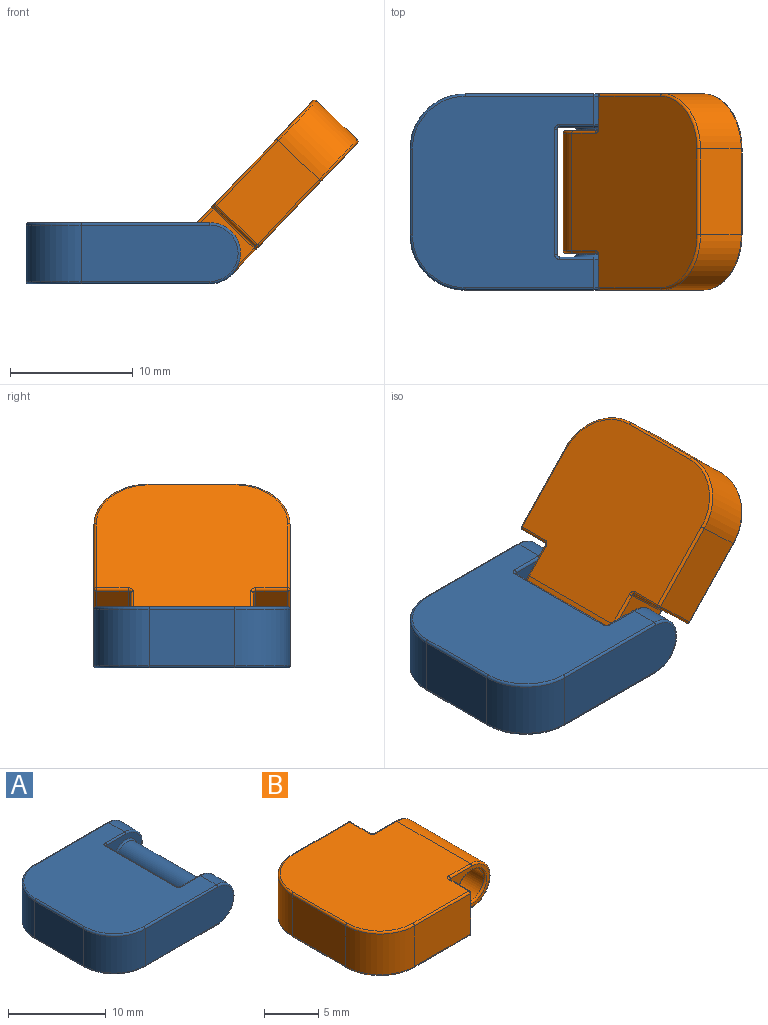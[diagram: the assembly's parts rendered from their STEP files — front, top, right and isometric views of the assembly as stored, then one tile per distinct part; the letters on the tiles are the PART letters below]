
ASSEMBLY  parts=2 mates=1
PART A: 41 faces, bbox 18.1x16.7x5.4 mm
  f0: plane 15.6x14.8mm, normal (0,0,-1), area 187.8mm2, adj f1,f8,f19,f21,f22,f23,f24,f29
  f1: cylinder r=2.5mm len=5mm, axis (0,1,0), area 18.1mm2, adj f0,f2,f17,f26
  f2: plane 15.6x14.8mm, normal (0,0,1), area 187.8mm2, adj f1,f8,f13,f14,f15,f16,f18,f27
  f3: plane 7x4.6mm, normal (-1,0,0), area 32.2mm2, adj f11,f12,f14,f23
  f4: plane 5.1x4.6mm, normal (0,-1,0), area 12.6mm2, adj f26,f27,f28,f29,f40
  f5: plane 12.8x4.6mm, normal (0,1,0), area 56.6mm2, adj f12,f15,f17,f19
  f6: plane 10.2x4.6mm, normal (1,0,0), area 46.9mm2, adj f28,f32,f33,f34
  f7: cylinder r=1.45mm len=10.2mm, axis (0,1,0), area 92.9mm2, adj f25,f40
  f8: cylinder r=2.5mm len=5mm, axis (0,-1,0), area 18.1mm2, adj f0,f2,f20,f39
  f9: plane 5.1x4.6mm, normal (0,1,0), area 12.6mm2, adj f25,f33,f37,f38,f39
  f10: plane 12.8x4.6mm, normal (0,-1,0), area 56.6mm2, adj f11,f18,f20,f22
  f11: cylinder r=4.5mm len=4.6mm, axis (0,0,-1), area 32.5mm2, adj f3,f10,f16,f24
  f12: cylinder r=4.5mm len=4.6mm, axis (0,0,-1), area 32.5mm2, adj f3,f5,f13,f21
  f13: torus R=4.3mm, axis (0,0,-1), area 2.2mm2, adj f2,f12,f14,f15
  f14: cylinder r=0.2mm len=7mm, axis (0,-1,0), area 2.2mm2, adj f2,f3,f13,f16
  f15: cylinder r=0.2mm len=10.5mm, axis (-1,0,0), area 3.3mm2, adj f2,f5,f13,f17
  f16: torus R=4.3mm, axis (0,0,-1), area 2.2mm2, adj f2,f11,f14,f18
  f17: torus R=2.3mm, axis (0,-1,0), area 2.4mm2, adj f1,f5,f15,f19
  f18: cylinder r=0.2mm len=10.5mm, axis (-1,0,0), area 3.3mm2, adj f2,f10,f16,f20
  f19: cylinder r=0.2mm len=10.5mm, axis (1,0,0), area 3.3mm2, adj f0,f5,f17,f21
  f20: torus R=2.3mm, axis (0,1,0), area 2.4mm2, adj f8,f10,f18,f22
  f21: torus R=4.3mm, axis (0,0,-1), area 2.2mm2, adj f0,f12,f19,f23
  f22: cylinder r=0.2mm len=10.5mm, axis (1,0,0), area 3.3mm2, adj f0,f10,f20,f24
  f23: cylinder r=0.2mm len=7mm, axis (0,1,0), area 2.2mm2, adj f0,f3,f21,f24
  f24: torus R=4.3mm, axis (0,0,-1), area 2.2mm2, adj f0,f11,f22,f23
  f25: torus R=1.65mm, axis (0,1,0), area 3mm2, adj f7,f9
  f26: torus R=2.3mm, axis (0,-1,0), area 2.4mm2, adj f1,f4,f27,f29
  f27: cylinder r=0.2mm len=2.8mm, axis (1,0,0), area 0.9mm2, adj f2,f4,f26,f30
  f28: cylinder r=0.2mm len=4.6mm, axis (0,0,-1), area 1.4mm2, adj f4,f6,f30,f31
  f29: cylinder r=0.2mm len=2.8mm, axis (-1,0,0), area 0.9mm2, adj f0,f4,f26,f31
  f30: torus R=0.4mm, axis (0,0,-1), area 0.1mm2, adj f2,f27,f28,f32
  f31: torus R=0.4mm, axis (0,0,-1), area 0.1mm2, adj f0,f28,f29,f34
  f32: cylinder r=0.2mm len=10.2mm, axis (0,-1,0), area 3.2mm2, adj f2,f6,f30,f35
  f33: cylinder r=0.2mm len=4.6mm, axis (0,0,-1), area 1.4mm2, adj f6,f9,f35,f36
  f34: cylinder r=0.2mm len=10.2mm, axis (0,1,0), area 3.2mm2, adj f0,f6,f31,f36
  f35: torus R=0.4mm, axis (0,0,-1), area 0.1mm2, adj f2,f32,f33,f37
  f36: torus R=0.4mm, axis (0,0,-1), area 0.1mm2, adj f0,f33,f34,f38
  f37: cylinder r=0.2mm len=2.8mm, axis (1,0,0), area 0.9mm2, adj f2,f9,f35,f39
  f38: cylinder r=0.2mm len=2.8mm, axis (-1,0,0), area 0.9mm2, adj f0,f9,f36,f39
  f39: torus R=2.3mm, axis (0,1,0), area 2.4mm2, adj f8,f9,f37,f38
  f40: torus R=1.65mm, axis (0,-1,0), area 3mm2, adj f4,f7
PART B: 47 faces, bbox 18.1x16.7x5.4 mm
  f0: plane 5.1x4.6mm, normal (0,-1,0), area 9.2mm2, adj f18,f25,f30,f31,f46
  f1: plane 5.1x4.6mm, normal (0,1,0), area 9.2mm2, adj f13,f14,f19,f20,f45
  f2: plane 15.6x14.8mm, normal (0,0,-1), area 203.8mm2, adj f3,f19,f26,f31,f32,f35,f38,f39
  f3: cylinder r=2.5mm len=9.6mm, axis (0,1,0), area 75.4mm2, adj f2,f4,f14,f25
  f4: plane 15.6x14.8mm, normal (0,0,1), area 203.8mm2, adj f3,f13,f15,f16,f17,f18,f21,f22
  f5: plane 7x4.6mm, normal (-1,0,0), area 32.2mm2, adj f11,f12,f17,f43
  f6: cylinder r=1.75mm len=9.6mm, axis (0,1,0), area 105.6mm2, adj f45,f46
  f7: plane 4.6x2.6mm, normal (1,0,0), area 12mm2, adj f20,f21,f32,f33
  f8: plane 7.3x4.6mm, normal (0,1,0), area 33.6mm2, adj f12,f22,f33,f39
  f9: plane 4.6x2.6mm, normal (1,0,0), area 12mm2, adj f29,f30,f37,f38
  f10: plane 7.3x4.6mm, normal (0,-1,0), area 33.6mm2, adj f11,f28,f37,f42
  f11: cylinder r=4.5mm len=4.6mm, axis (0,0,-1), area 32.5mm2, adj f5,f10,f23,f44
  f12: cylinder r=4.5mm len=4.6mm, axis (0,0,-1), area 32.5mm2, adj f5,f8,f16,f41
  f13: cylinder r=0.2mm len=2.8mm, axis (-1,0,0), area 0.9mm2, adj f1,f4,f14,f15
  f14: torus R=2.3mm, axis (0,-1,0), area 2.4mm2, adj f1,f3,f13,f19
  f15: torus R=0.4mm, axis (0,0,-1), area 0.1mm2, adj f4,f13,f20,f21
  f16: torus R=4.3mm, axis (0,0,-1), area 2.2mm2, adj f4,f12,f17,f22
  f17: cylinder r=0.2mm len=7mm, axis (0,-1,0), area 2.2mm2, adj f4,f5,f16,f23
  f18: cylinder r=0.2mm len=2.8mm, axis (1,0,0), area 0.9mm2, adj f0,f4,f24,f25
  f19: cylinder r=0.2mm len=2.8mm, axis (1,0,0), area 0.9mm2, adj f1,f2,f14,f26
  f20: cylinder r=0.2mm len=4.6mm, axis (0,0,1), area 1.4mm2, adj f1,f7,f15,f26
  f21: cylinder r=0.2mm len=2.6mm, axis (0,-1,0), area 0.8mm2, adj f4,f7,f15,f27
  f22: cylinder r=0.2mm len=7.3mm, axis (-1,0,0), area 2.3mm2, adj f4,f8,f16,f27
  f23: torus R=4.3mm, axis (0,0,-1), area 2.2mm2, adj f4,f11,f17,f28
  f24: torus R=0.4mm, axis (0,0,-1), area 0.1mm2, adj f4,f18,f29,f30
  f25: torus R=2.3mm, axis (0,-1,0), area 2.4mm2, adj f0,f3,f18,f31
  f26: torus R=0.4mm, axis (0,0,-1), area 0.1mm2, adj f2,f19,f20,f32
  f27: sphere r=0.2mm, area 0.1mm2, adj f21,f22,f33
  f28: cylinder r=0.2mm len=7.3mm, axis (-1,0,0), area 2.3mm2, adj f4,f10,f23,f34
  f29: cylinder r=0.2mm len=2.6mm, axis (0,-1,0), area 0.8mm2, adj f4,f9,f24,f34
  f30: cylinder r=0.2mm len=4.6mm, axis (0,0,1), area 1.4mm2, adj f0,f9,f24,f35
  f31: cylinder r=0.2mm len=2.8mm, axis (-1,0,0), area 0.9mm2, adj f0,f2,f25,f35
  f32: cylinder r=0.2mm len=2.6mm, axis (0,1,0), area 0.8mm2, adj f2,f7,f26,f36
  f33: cylinder r=0.2mm len=4.6mm, axis (0,0,-1), area 1.4mm2, adj f7,f8,f27,f36
  f34: sphere r=0.2mm, area 0.1mm2, adj f28,f29,f37
  f35: torus R=0.4mm, axis (0,0,-1), area 0.1mm2, adj f2,f30,f31,f38
  f36: sphere r=0.2mm, area 0.1mm2, adj f32,f33,f39
  f37: cylinder r=0.2mm len=4.6mm, axis (0,0,1), area 1.4mm2, adj f9,f10,f34,f40
  f38: cylinder r=0.2mm len=2.6mm, axis (0,1,0), area 0.8mm2, adj f2,f9,f35,f40
  f39: cylinder r=0.2mm len=7.3mm, axis (1,0,0), area 2.3mm2, adj f2,f8,f36,f41
  f40: sphere r=0.2mm, area 0.1mm2, adj f37,f38,f42
  f41: torus R=4.3mm, axis (0,0,-1), area 2.2mm2, adj f2,f12,f39,f43
  f42: cylinder r=0.2mm len=7.3mm, axis (1,0,0), area 2.3mm2, adj f2,f10,f40,f44
  f43: cylinder r=0.2mm len=7mm, axis (0,1,0), area 2.2mm2, adj f2,f5,f41,f44
  f44: torus R=4.3mm, axis (0,0,-1), area 2.2mm2, adj f2,f11,f42,f43
  f45: torus R=1.95mm, axis (0,-1,0), area 3.6mm2, adj f1,f6
  f46: torus R=1.95mm, axis (0,-1,0), area 3.6mm2, adj f0,f6
PLACE A at identity fixed
PLACE B rot(axis=(0,1,0),133.6deg) t=(-1.81,-3,4.23)mm
MATE revolute A.f7 <-> B.f3  axis (0,1,0) through (0,-8,2.5)mm
